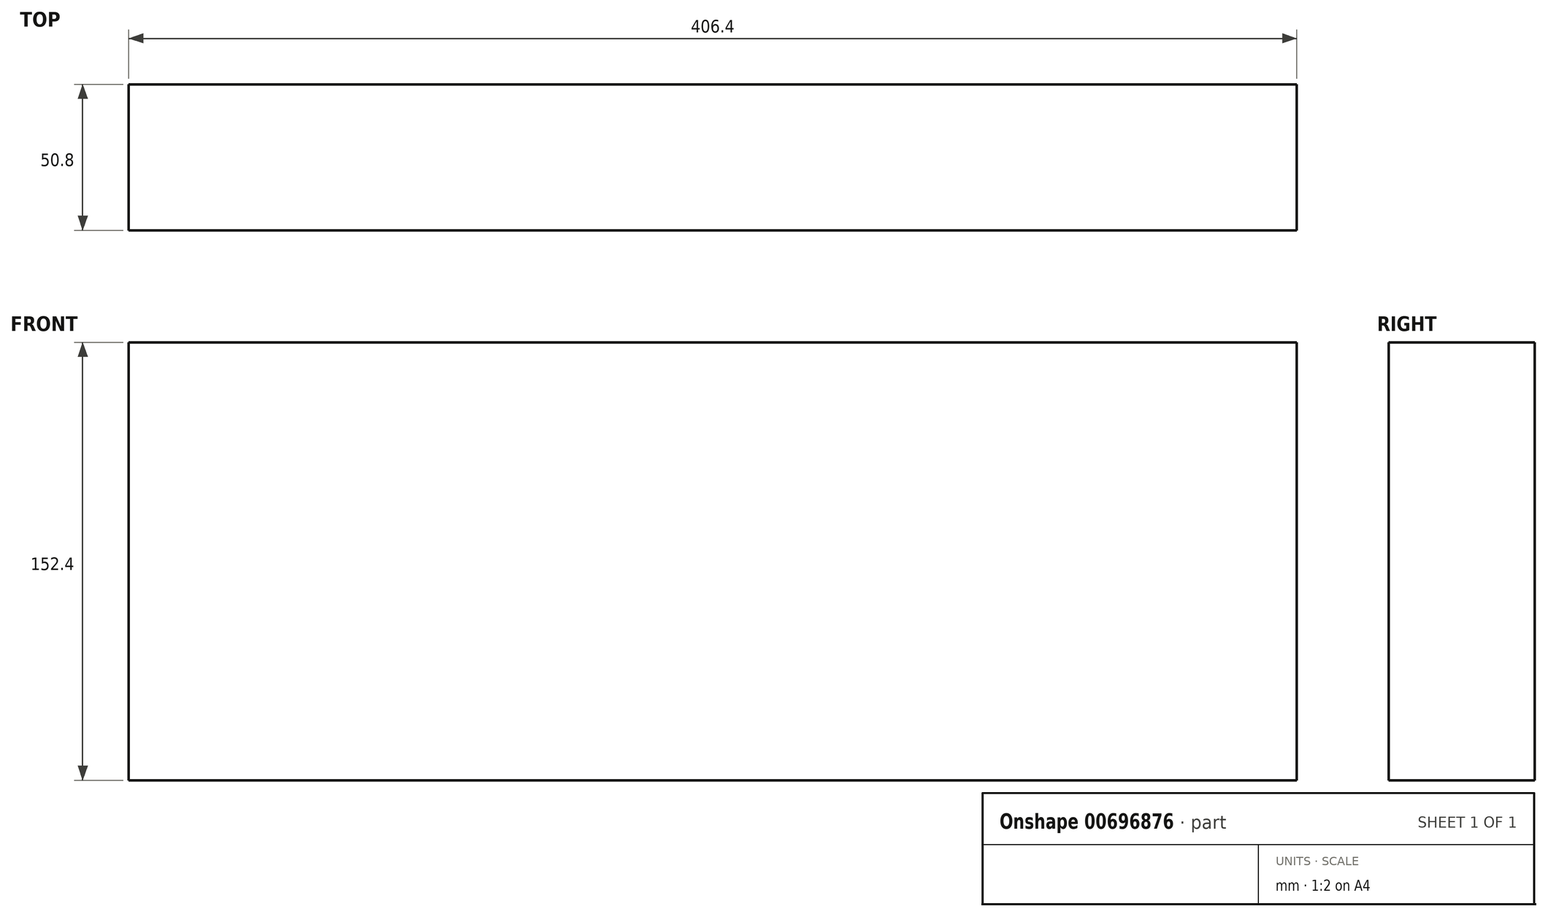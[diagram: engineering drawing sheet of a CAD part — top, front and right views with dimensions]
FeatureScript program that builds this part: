
annotation { "Feature Type Name" : "Feature", "Feature Type Description" : "" }
export const myFeature = defineFeature(function(context is Context, id is Id, definition is map)
    precondition{}
    {
        {
            var Q0;
            Q0=qCreatedBy(makeId("Top.planeOp"),FACE);
            var sketch = newSketch(context, id + "F0", { "sketchPlane" : qUnion([Q0])});
            skLineSegment(sketch, "E0.bottom", {"start": v(0, 0) * mm, "end": v(406.4, 0) * mm});
            skLineSegment(sketch, "E0.top", {"start": v(0, -50.8) * mm, "end": v(406.4, -50.8) * mm});
            skLineSegment(sketch, "E0.left", {"start": v(0, 0) * mm, "end": v(0, -50.8) * mm});
            skLineSegment(sketch, "E0.right", {"start": v(406.4, 0) * mm, "end": v(406.4, -50.8) * mm});
            skSolve(sketch);
        }
        {
            var Q0;
            Q0=makeQuery(id+"F0.imprint","IMPRINT",FACE,{"disambiguationData":[TD([[makeQuery(id+"F0.imprint","IMPRINT",EDGE,{"derivedFrom":sQuery(id+"F0.wireOp",EDGE,"E0.bottom")}),-1.0]])]});
            extrude(context, id + "F1", {"entities" : qUnion([Q0]), "oppositeDirection" : true, "depth" : 152.4 * mm, "offsetDistance" : 25.4 * mm});
        }
    });
